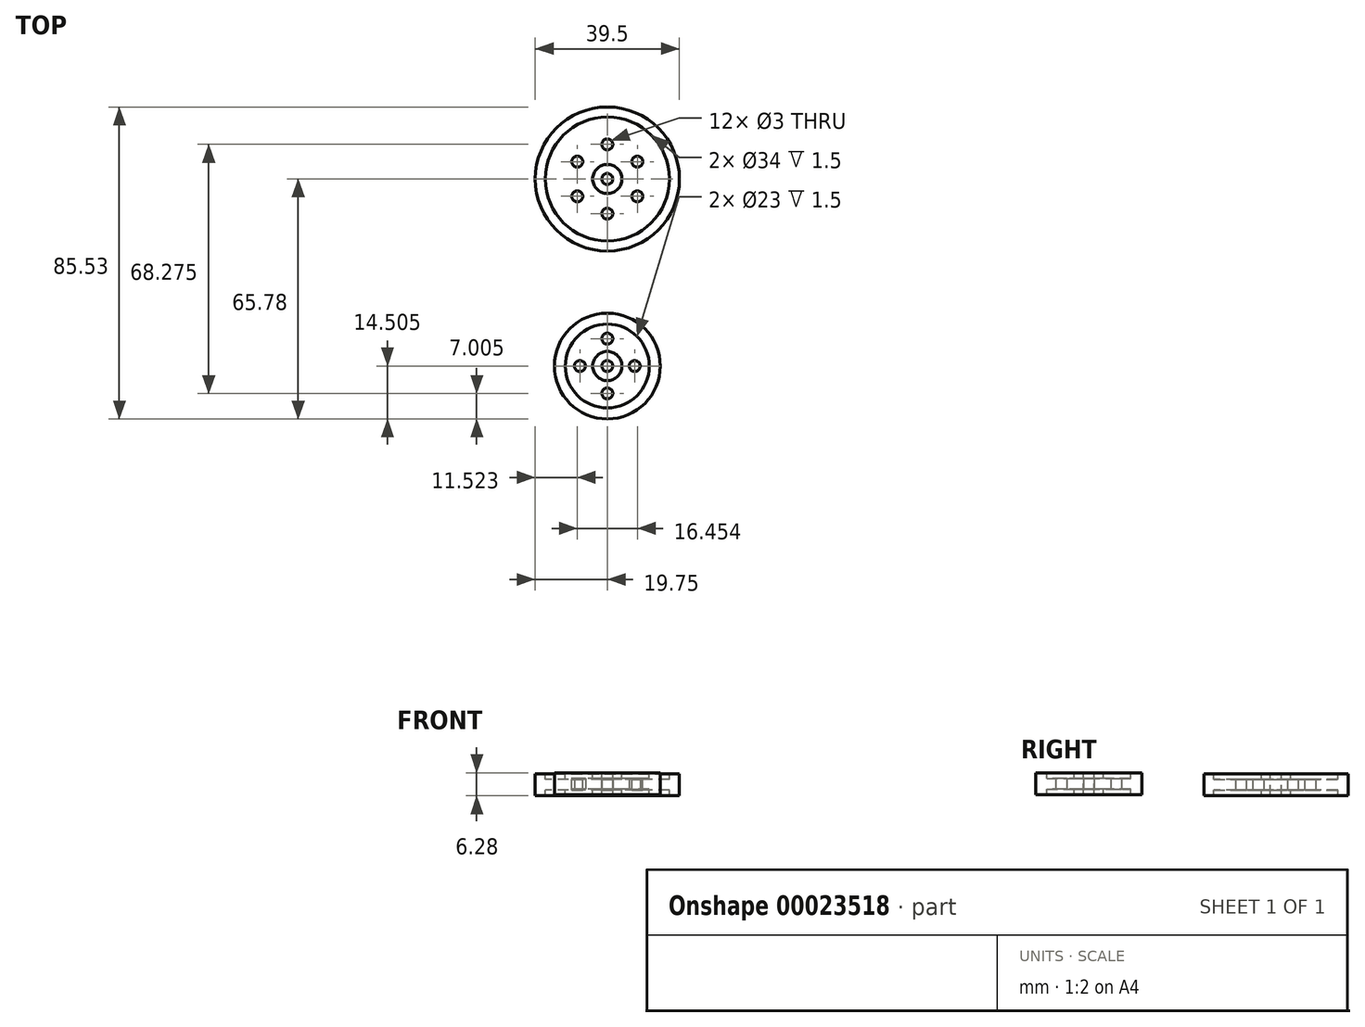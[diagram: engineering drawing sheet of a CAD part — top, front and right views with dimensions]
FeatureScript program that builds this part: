
annotation { "Feature Type Name" : "Feature", "Feature Type Description" : "" }
export const myFeature = defineFeature(function(context is Context, id is Id, definition is map)
    precondition{}
    {
        {
            var Q0;
            Q0=qCreatedBy(makeId("Front.planeOp"),FACE);
            var sketch = newSketch(context, id + "F0", { "sketchPlane" : qUnion([Q0])});
            skLineSegment(sketch, "E0", {"start": v(0, 6.94) * mm, "end": v(0, -7.29) * mm, "construction": true});
            skLineSegment(sketch, "E1.bottom", {"start": v(1.5, 3.23) * mm, "end": v(4, 3.23) * mm});
            skLineSegment(sketch, "E1.top", {"start": v(1.5, -2.77) * mm, "end": v(4, -2.77) * mm});
            skLineSegment(sketch, "E1.left", {"start": v(1.5, 3.23) * mm, "end": v(1.5, -2.77) * mm});
            skLineSegment(sketch, "E1.right", {"start": v(4, 3.23) * mm, "end": v(4, -2.77) * mm});
            skLineSegment(sketch, "E2.bottom", {"start": v(4, 1.73) * mm, "end": v(17, 1.73) * mm});
            skLineSegment(sketch, "E2.top", {"start": v(4, -1.27) * mm, "end": v(17, -1.27) * mm});
            skLineSegment(sketch, "E2.left", {"start": v(4, 1.73) * mm, "end": v(4, -1.27) * mm});
            skLineSegment(sketch, "E2.right", {"start": v(17, 1.73) * mm, "end": v(17, -1.27) * mm});
            skLineSegment(sketch, "E3.bottom", {"start": v(17, 3.23) * mm, "end": v(19.75, 3.23) * mm});
            skLineSegment(sketch, "E3.top", {"start": v(17, -2.77) * mm, "end": v(19.75, -2.77) * mm});
            skLineSegment(sketch, "E3.left", {"start": v(17, 3.23) * mm, "end": v(17, -2.77) * mm});
            skLineSegment(sketch, "E3.right", {"start": v(19.75, 3.23) * mm, "end": v(19.75, -2.77) * mm});
            skSolve(sketch);
        }
        {
            var Q0;
            {var subQ3=sQuery(id+"F0.wireOp",EDGE,"E1.bottom");Q0=makeQuery(id+"F0.imprint","IMPRINT",FACE,{"disambiguationData":[TD([[makeQuery(id+"F0.imprint","IMPRINT",EDGE,{"derivedFrom":subQ3}),-1.0]])]});}
            var Q1;
            {var subQ2=sQuery(id+"F0.wireOp",EDGE,"E2.bottom");Q1=makeQuery(id+"F0.imprint","IMPRINT",FACE,{"disambiguationData":[TD([[makeQuery(id+"F0.imprint","IMPRINT",EDGE,{"derivedFrom":subQ2}),-1.0]])]});}
            var Q2;
            {var subQ4=sQuery(id+"F0.wireOp",EDGE,"E3.bottom");Q2=makeQuery(id+"F0.imprint","IMPRINT",FACE,{"disambiguationData":[TD([[makeQuery(id+"F0.imprint","IMPRINT",EDGE,{"derivedFrom":subQ4}),-1.0]])]});}
            var Q3;
            Q3=sQuery(id+"F0.wireOp",EDGE,"E0");
            revolve(context, id + "F1", {"entities" : qUnion([Q0, Q1, Q2]), "axis" : qUnion([Q3]), "revolveType" : RevolveType.FULL});
        }
        {
            var Q0;
            Q0=makeQuery(id+"F1.opRevolve","SWEPT_FACE",FACE,{"disambiguationData":[OSD([sQuery(id+"F0.wireOp",EDGE,"E2.bottom")])]});
            var sketch = newSketch(context, id + "F2", { "sketchPlane" : qUnion([Q0])});
            skCircle(sketch, "E4", {"center": v(0, 9.5) * mm, "radius": 1.5 * mm});
            skSolve(sketch);
        }
        {
            var Q0;
            Q0=makeQuery(id+"F2.imprint","IMPRINT",FACE,{"disambiguationData":[TD([[makeQuery(id+"F2.imprint","IMPRINT",EDGE,{"derivedFrom":sQuery(id+"F2.wireOp",EDGE,"E4")}),1.0]])]});
            extrude(context, id + "F3", {"entities" : qUnion([Q0]), "operationType" : NewBodyOperationType.REMOVE, "oppositeDirection" : true, "depth" : 2286 * mm});
        }
        {
            var Q0;
            Q0=makeQuery(id+"F3.boolean.opBoolean","COPY",FACE,{"derivedFrom":makeQuery(id+"F3.opExtrude","SWEPT_FACE",FACE,{"disambiguationData":[OSD([sQuery(id+"F2.wireOp",EDGE,"E4")])]})});
            var Q1;
            Q1=makeQuery(id+"F1.opRevolve","SWEPT_EDGE",EDGE,{"disambiguationData":[OSD([sQuery(id+"F0.wireOp",EDGE,"E1.bottom"),sQuery(id+"F0.wireOp",EDGE,"E1.left")])]});
            circularPattern(context, id + "F4", {"faces" : qUnion([Q0]), "axis" : qUnion([Q1]), "angle" : 360 * degree, "instanceCount" : 6, "equalSpace" : true, "patternType" : PatternType.FACE});
        }
        {
            var Q0;
            Q0=qCreatedBy(makeId("Right.planeOp"),FACE);
            var sketch = newSketch(context, id + "F5", { "sketchPlane" : qUnion([Q0])});
            skLineSegment(sketch, "E5", {"start": v(-51.28, 22.97) * mm, "end": v(-51.28, -35.22) * mm, "construction": true});
            skLineSegment(sketch, "E6.bottom", {"start": v(-49.78, 3.51) * mm, "end": v(-47.28, 3.51) * mm});
            skLineSegment(sketch, "E6.top", {"start": v(-49.78, -2.49) * mm, "end": v(-47.28, -2.49) * mm});
            skLineSegment(sketch, "E6.left", {"start": v(-49.78, 3.51) * mm, "end": v(-49.78, -2.49) * mm});
            skLineSegment(sketch, "E6.right", {"start": v(-47.28, 3.51) * mm, "end": v(-47.28, -2.49) * mm});
            skLineSegment(sketch, "E7.bottom", {"start": v(-47.28, 2.01) * mm, "end": v(-39.78, 2.01) * mm});
            skLineSegment(sketch, "E7.top", {"start": v(-47.28, -0.99) * mm, "end": v(-39.78, -0.99) * mm});
            skLineSegment(sketch, "E7.left", {"start": v(-47.28, 2.01) * mm, "end": v(-47.28, -0.99) * mm});
            skLineSegment(sketch, "E7.right", {"start": v(-39.78, 2.01) * mm, "end": v(-39.78, -0.99) * mm});
            skLineSegment(sketch, "E8.bottom", {"start": v(-39.78, 3.51) * mm, "end": v(-36.78, 3.51) * mm});
            skLineSegment(sketch, "E8.top", {"start": v(-39.78, -2.49) * mm, "end": v(-36.78, -2.49) * mm});
            skLineSegment(sketch, "E8.left", {"start": v(-39.78, 3.51) * mm, "end": v(-39.78, -2.49) * mm});
            skLineSegment(sketch, "E8.right", {"start": v(-36.78, 3.51) * mm, "end": v(-36.78, -2.49) * mm});
            skSolve(sketch);
        }
        {
            var Q0;
            {var subQ3=sQuery(id+"F5.wireOp",EDGE,"E6.bottom");Q0=makeQuery(id+"F5.imprint","IMPRINT",FACE,{"disambiguationData":[TD([[makeQuery(id+"F5.imprint","IMPRINT",EDGE,{"derivedFrom":subQ3}),-1.0]])]});}
            var Q1;
            {var subQ2=sQuery(id+"F5.wireOp",EDGE,"E7.bottom");Q1=makeQuery(id+"F5.imprint","IMPRINT",FACE,{"disambiguationData":[TD([[makeQuery(id+"F5.imprint","IMPRINT",EDGE,{"derivedFrom":subQ2}),-1.0]])]});}
            var Q2;
            {var subQ4=sQuery(id+"F5.wireOp",EDGE,"E8.bottom");Q2=makeQuery(id+"F5.imprint","IMPRINT",FACE,{"disambiguationData":[TD([[makeQuery(id+"F5.imprint","IMPRINT",EDGE,{"derivedFrom":subQ4}),-1.0]])]});}
            var Q3;
            Q3=sQuery(id+"F5.wireOp",EDGE,"E5");
            revolve(context, id + "F6", {"entities" : qUnion([Q0, Q1, Q2]), "axis" : qUnion([Q3]), "revolveType" : RevolveType.FULL});
        }
        {
            var Q0;
            Q0=makeQuery(id+"F6.opRevolve","SWEPT_FACE",FACE,{"disambiguationData":[OSD([sQuery(id+"F5.wireOp",EDGE,"E7.top")])]});
            var sketch = newSketch(context, id + "F7", { "sketchPlane" : qUnion([Q0])});
            skLineSegment(sketch, "E9", {"start": v(0, 51.28) * mm, "end": v(13.94, 51.28) * mm, "construction": true});
            skCircle(sketch, "E10", {"center": v(7.5, 51.28) * mm, "radius": 1.5 * mm});
            skSolve(sketch);
        }
        {
            var Q0;
            Q0=makeQuery(id+"F7.imprint","IMPRINT",FACE,{"disambiguationData":[TD([[makeQuery(id+"F7.imprint","IMPRINT",EDGE,{"derivedFrom":sQuery(id+"F7.wireOp",EDGE,"E10")}),1.0]])]});
            extrude(context, id + "F8", {"entities" : qUnion([Q0]), "operationType" : NewBodyOperationType.REMOVE, "endBound" : BoundingType.THROUGH_ALL, "oppositeDirection" : true, "depth" : 25.4 * mm});
        }
        {
            var Q0;
            Q0=makeQuery(id+"F6.opRevolve","SWEPT_BODY",BODY,{"disambiguationData":[OSD([sQuery(id+"F5.wireOp",EDGE,"E6.bottom"),sQuery(id+"F5.wireOp",EDGE,"E6.top"),sQuery(id+"F5.wireOp",EDGE,"E6.left"),sQuery(id+"F5.wireOp",EDGE,"E6.right"),sQuery(id+"F5.wireOp",EDGE,"E7.bottom"),sQuery(id+"F5.wireOp",EDGE,"E7.top"),sQuery(id+"F5.wireOp",EDGE,"E8.bottom"),sQuery(id+"F5.wireOp",EDGE,"E8.top"),sQuery(id+"F5.wireOp",EDGE,"E8.left"),sQuery(id+"F5.wireOp",EDGE,"E8.right")])]});
            var Q1;
            Q1=makeQuery(id+"F8.boolean.opBoolean","COPY",FACE,{"derivedFrom":makeQuery(id+"F8.opExtrude","SWEPT_FACE",FACE,{"disambiguationData":[OSD([sQuery(id+"F7.wireOp",EDGE,"E10")])]})});
            var Q2;
            Q2=makeQuery(id+"F6.opRevolve","SWEPT_FACE",FACE,{"disambiguationData":[OSD([sQuery(id+"F5.wireOp",EDGE,"E6.left")])]});
            circularPattern(context, id + "F9", {"faces" : qUnion([Q1]), "axis" : qUnion([Q2]), "angle" : 360 * degree, "instanceCount" : 4, "equalSpace" : true, "patternType" : PatternType.FACE});
        }
    });
